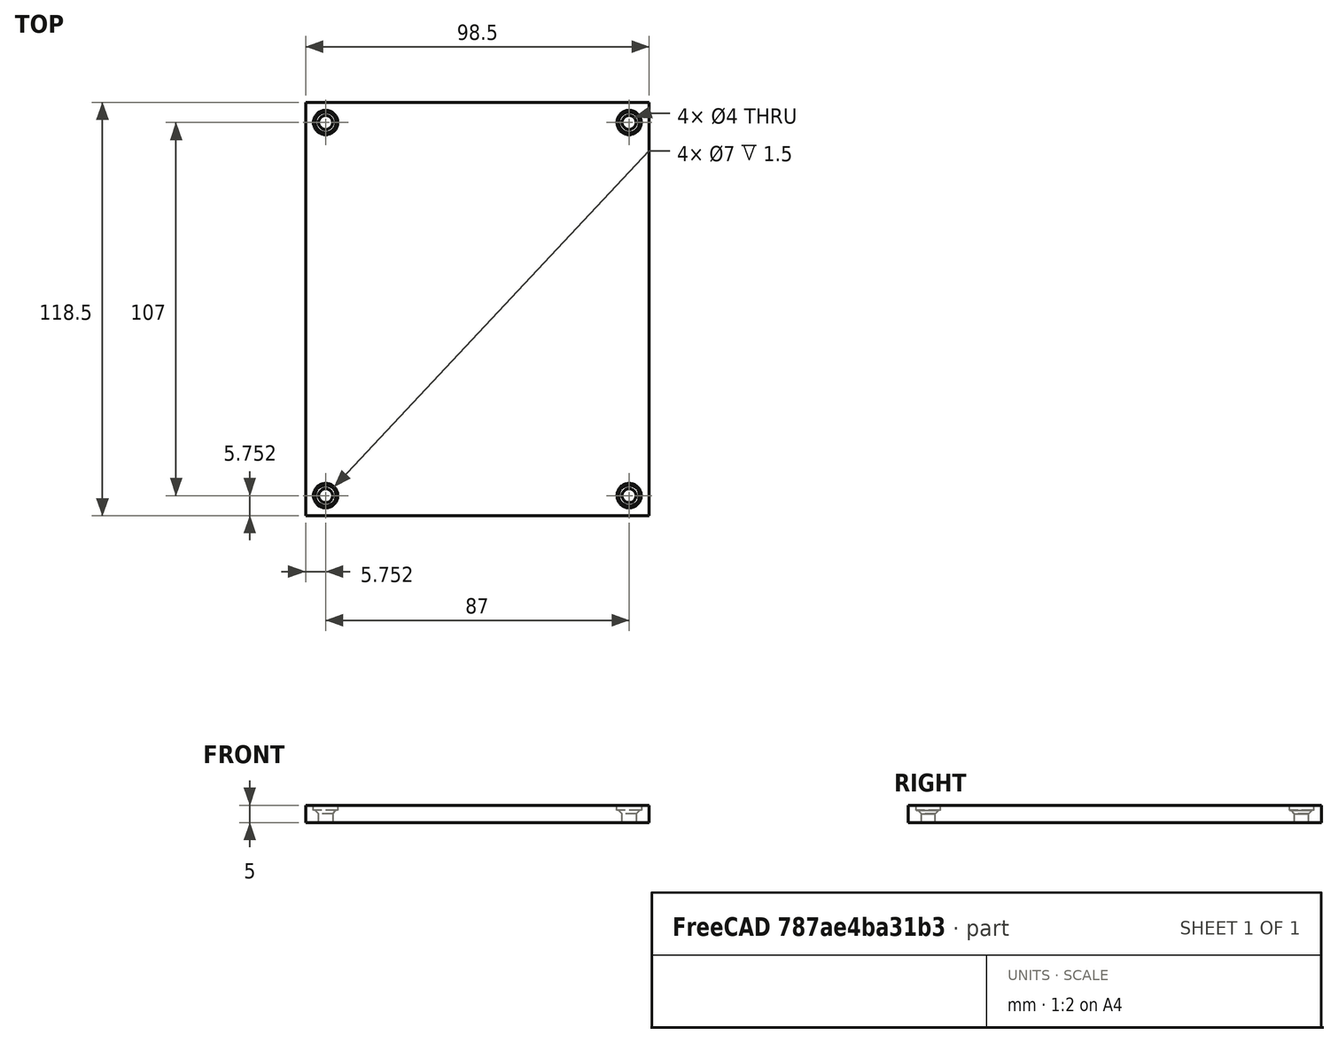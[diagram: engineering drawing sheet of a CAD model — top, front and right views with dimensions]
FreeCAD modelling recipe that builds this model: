
FCSTD DOCUMENT  (FreeCAD 0.17R13541 (Git))
Label: Bottom
License: All rights reserved
LicenseURL: http://en.wikipedia.org/wiki/All_rights_reserved
objects: Sketcher::SketchObject×3, PartDesign::Pocket×2, PartDesign::Pad×1, PartDesign::Chamfer×1, PartDesign::Body×1, Mesh::Feature×1
note: 11 computed .brp shape members not serialized (recipe doc carries the construction recipe); baked Part::Feature solids carry a one-line shape summary decoded from their .brp

FEATURE [Sketcher::SketchObject] Sketch
  MapMode = 5
  Support = -> [XY_Plane]
  sketch-geometry (4):
    g0: LineSegment StartX=-36.6679 StartY=86.3024 StartZ=0 EndX=61.8321 EndY=86.3024 EndZ=0
    g1: LineSegment StartX=61.8321 StartY=86.3024 StartZ=0 EndX=61.8321 EndY=-32.1976 EndZ=0
    g2: LineSegment StartX=61.8321 StartY=-32.1976 StartZ=0 EndX=-36.6679 EndY=-32.1976 EndZ=0
    g3: LineSegment StartX=-36.6679 StartY=-32.1976 StartZ=0 EndX=-36.6679 EndY=86.3024 EndZ=0
  constraints (10):
    c: Coincident(g0,g1)
    c: Coincident(g1,g2)
    c: Coincident(g2,g3)
    c: Coincident(g3,g0)
    c: Horizontal(g0)
    c: Horizontal(g2)
    c: Vertical(g1)
    c: Vertical(g3)
    c: DistanceX(g0,g0) = 98.5
    c: DistanceY(g3,g3) = 118.5
FEATURE [PartDesign::Pad] Pad
  Length = 5
  Length2 = 100
  Profile = -> Sketch
  Type = 0
FEATURE [Sketcher::SketchObject] Sketch001
  ExternalGeometry = -> [Pad]
  MapMode = 5
  Placement = pos=(0,0,5) rot=(0,0,1;0rad)
  Support = -> [Pad]
  sketch-geometry (4):
    g0: Circle CenterX=-30.9179 CenterY=80.5524 CenterZ=0 NormalX=0 NormalY=0 NormalZ=1 AngleXU=0 Radius=3.5
    g1: Circle CenterX=56.0821 CenterY=80.5524 CenterZ=0 NormalX=0 NormalY=0 NormalZ=1 AngleXU=0 Radius=3.5
    g2: Circle CenterX=56.0821 CenterY=-26.4476 CenterZ=0 NormalX=0 NormalY=0 NormalZ=1 AngleXU=0 Radius=3.5
    g3: Circle CenterX=-30.9179 CenterY=-26.4476 CenterZ=0 NormalX=0 NormalY=0 NormalZ=1 AngleXU=0 Radius=3.5
  constraints (12):
    c: DistanceX(g-4,g0) = 5.75
    c: DistanceX(g1,g-3) = 5.75
    c: DistanceX(g-5,g3) = 5.75
    c: DistanceX(g2,g-6) = 5.75
    c: DistanceY(g0,g-4) = 5.75
    c: DistanceY(g1,g-3) = 5.75
    c: DistanceY(g-5,g3) = 5.75
    c: DistanceY(g-6,g2) = 5.75
    c: Radius(g0) = 3.5
    c: Radius(g1) = 3.5
    c: Radius(g3) = 3.5
    c: Radius(g2) = 3.5
FEATURE [PartDesign::Pocket] Pocket
  BaseFeature = -> Pad
  Length = 1.5
  Length2 = 100
  Profile = -> Sketch001
  Type = 0
FEATURE [Sketcher::SketchObject] Sketch002
  ExternalGeometry = -> [Pocket]
  MapMode = 5
  Placement = pos=(0,0,5) rot=(0,0,1;0rad)
  Support = -> [Pocket]
  sketch-geometry (4):
    g0: Circle CenterX=-30.9179 CenterY=80.5524 CenterZ=0 NormalX=0 NormalY=0 NormalZ=1 AngleXU=0 Radius=2
    g1: Circle CenterX=56.0821 CenterY=80.5524 CenterZ=0 NormalX=0 NormalY=0 NormalZ=1 AngleXU=0 Radius=2
    g2: Circle CenterX=-30.9179 CenterY=-26.4476 CenterZ=0 NormalX=0 NormalY=0 NormalZ=1 AngleXU=0 Radius=2
    g3: Circle CenterX=56.0821 CenterY=-26.4476 CenterZ=0 NormalX=0 NormalY=0 NormalZ=1 AngleXU=0 Radius=2
  constraints (8):
    c: Radius(g1) = 2
    c: Radius(g0) = 2
    c: Radius(g2) = 2
    c: Radius(g3) = 2
    c: Coincident(g0,g-3)
    c: Coincident(g1,g-4)
    c: Coincident(g3,g-6)
    c: Coincident(g-5,g2)
FEATURE [PartDesign::Pocket] Pocket001
  BaseFeature = -> Pocket
  Length = 5
  Length2 = 100
  Profile = -> Sketch002
  Type = 0
FEATURE [PartDesign::Chamfer] Chamfer
  Base = -> Pocket001 [Edge27,Edge25,Edge23,Edge21]
  BaseFeature = -> Pocket001
  Size = 1
FEATURE [PartDesign::Body] Body
  Group = -> [Sketch,Pad,Sketch001,Pocket,Sketch002,Pocket001,Chamfer]
  Origin = -> Origin
  Tip = -> Chamfer
FEATURE [Mesh::Feature] Mesh  label="Bottom"
